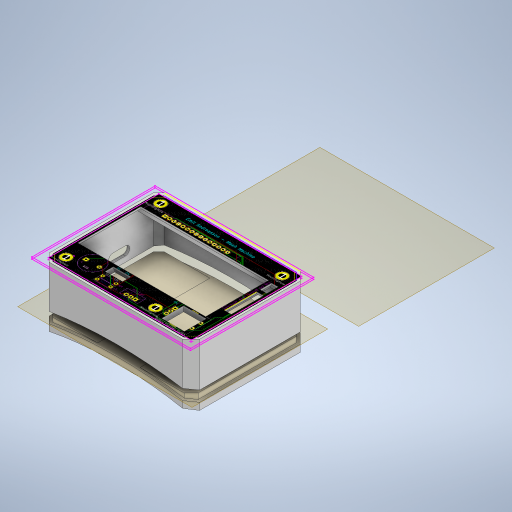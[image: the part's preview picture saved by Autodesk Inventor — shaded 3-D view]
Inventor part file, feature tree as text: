
AUTODESK INVENTOR PART (.ipt)
format: ipt  version: 2024 (Build 280153000, 153)  size: 747,008 bytes
history: native  units: mm
features: sketch x15, extrude x12, projected_geometry x5, plane x3, other x3
ambient origin geometry x8: Origin, YZ Plane, XZ Plane, XY Plane, X Axis, Y Axis, Z Axis, Center Point
bodies: Solid9 (feature_tree)
feature tree (38):
  extrude  "Extrusion14"  Depth=70.0mm
  plane  "Work Plane8"
  sketch  "Sketch23"  dims[d602=1.0mm d603=0.0mm d633=39.25mm]
  sketch  "3D Sketch1"
  other  "Decal3"
  extrude  "Extrusion16"  Depth=1.0mm
  extrude  "Extrusion17"  TaperAngle=45.0deg  [1 undecoded]
  extrude  "Extrusion18"  TaperAngle=135.0deg  [1 undecoded]
  sketch  "Sketch27"  dims[d686=0.5mm d687=0.5mm]
  extrude  "Extrusion20"  Depth=0.5mm
  extrude  "Extrusion21"  Depth=0.5mm
  extrude  "Extrusion22"  TaperAngle=135.0deg  [1 undecoded]
  extrude  "Extrusion23"  TaperAngle=135.0deg  [1 undecoded]
  sketch  "Sketch31"  dims[d698=1.5mm d699=1.5mm]
  plane  "Work Plane10"
  extrude  "Extrusion24"  Depth=1.5mm
  extrude  "Extrusion25"  Depth=1.5mm
  plane  "Work Plane11"
  extrude  "Extrusion26"  Depth=1.5mm TaperAngle=0.0deg
  extrude  "Extrusion27"  Depth=2.5mm
  sketch  "Sketch21"  dims[d597=90.0mm d598=70.0mm]
  other  "Image15"
  sketch  "Sketch24"  dims[d668=62.75mm d681=45.0deg]
  projected_geometry  "Projected Loop3"
  projected_geometry  "Projected Loop4"
  projected_geometry  "Projected Loop5"
  projected_geometry  "Projected Loop6"
  projected_geometry  "Projected Loop7"
  other  "Project from Sketch23"
  sketch  "Sketch25"  dims[d682=135.0deg d683=135.0deg]
  sketch  "Sketch26"  dims[d684=135.0deg d685=0.5mm]
  sketch  "Sketch28"  dims[d688=0.5mm d693=135.0deg]
  sketch  "Sketch29"  dims[d694=135.0deg d695=135.0deg]
  sketch  "Sketch30"  dims[d696=135.0deg d697=1.5mm]
  sketch  "Sketch32"  dims[d700=1.5mm d703=25.0mm d704=0.0mm]
  sketch  "Sketch33"  dims[d705=24.0mm d706=0.0mm d707=2.5mm]
  sketch  "Sketch34"  dims[d708=2.5mm]
  sketch  "Sketch35"  dims[d709=2.5mm d710=2.5mm d711=8.0mm d712=0.0mm d715=12.0mm d716=5.0mm d721=18.1mm d722=10.0mm d723=0.0mm d724=81.103353mm d725=25.0mm d726=0.0mm d728=2.0mm d729=0.0mm d730=1.0mm d731=1.0mm d733=24.0mm d735=240.0mm d736=0.0mm d737=0.0mm d738=1.0mm d739=1.0mm d740=1.0mm d742=90.0deg d743=10.0mm d744=0.0mm d746=4.0mm d747=240.0mm d748=10.0mm d749=0.0mm d750=90.0deg d751=3.5mm d752=0.0mm d753=4.0mm d754=0.0mm d727=0.5mm]
note: 4 required parameter values undecoded (feature->parameter linkage not recoverable at this tier; creation-order binding heuristic only, values carry confidence <= 0.55)
